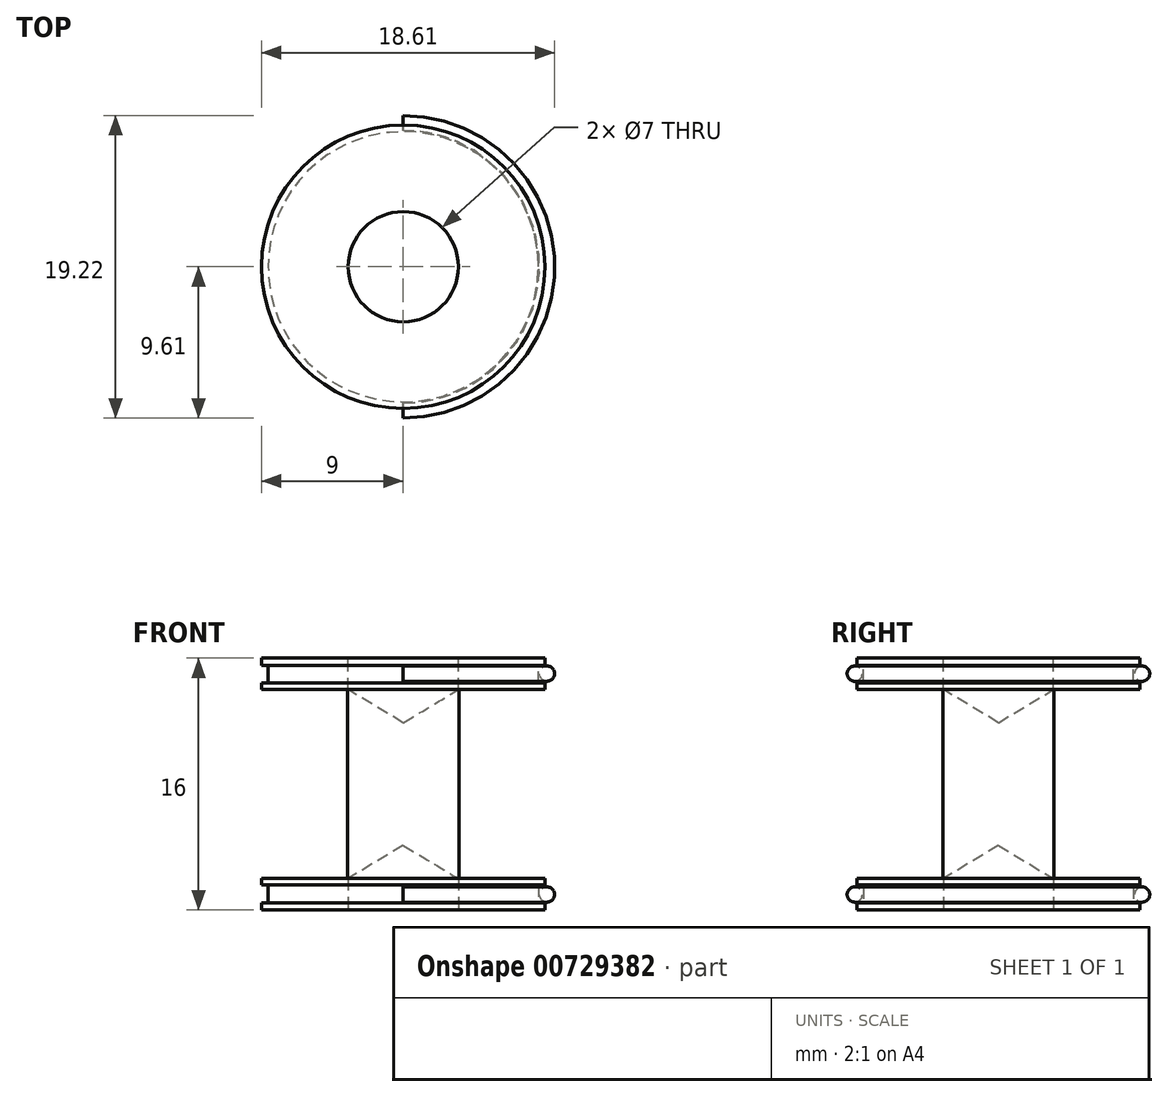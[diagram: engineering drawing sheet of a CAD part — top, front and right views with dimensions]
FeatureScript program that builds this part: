
annotation { "Feature Type Name" : "Feature", "Feature Type Description" : "" }
export const myFeature = defineFeature(function(context is Context, id is Id, definition is map)
    precondition{}
    {
        {
            var Q0;
            Q0=qCreatedBy(makeId("Top.planeOp"),FACE);
            var sketch = newSketch(context, id + "F0", { "sketchPlane" : qUnion([Q0])});
            skCircle(sketch, "E0", {"center": v(0, 0) * mm, "radius": 9 * mm});
            skSolve(sketch);
        }
        {
            var Q0;
            Q0=makeQuery(id+"F0.imprint","IMPRINT",FACE,{"disambiguationData":[TD([[makeQuery(id+"F0.imprint","IMPRINT",EDGE,{"derivedFrom":sQuery(id+"F0.wireOp",EDGE,"E0")}),1.0]])]});
            extrude(context, id + "F1", {"entities" : qUnion([Q0]), "depth" : 2 * mm, "offsetDistance" : 25 * mm});
        }
        {
            var Q0;
            Q0=qCreatedBy(makeId("Right.planeOp"),FACE);
            var sketch = newSketch(context, id + "F2", { "sketchPlane" : qUnion([Q0])});
            skLineSegment(sketch, "E1.bottom", {"start": v(8.58, 1.53) * mm, "end": v(9.56, 1.53) * mm});
            skLineSegment(sketch, "E1.top", {"start": v(8.58, 0.42) * mm, "end": v(9.56, 0.42) * mm});
            skLineSegment(sketch, "E1.left", {"start": v(8.58, 1.53) * mm, "end": v(8.58, 0.42) * mm});
            skLineSegment(sketch, "E1.right", {"start": v(9.56, 1.53) * mm, "end": v(9.56, 0.42) * mm});
            skSolve(sketch);
        }
        {
            var Q0;
            Q0=qCreatedBy(makeId("Top.planeOp"),FACE);
            cPlane(context, id + "F3", {"entities" : qUnion([Q0]), "cplaneType" : CPlaneType.OFFSET, "offset" : 1 * mm, "width" : 150 * mm, "height" : 150 * mm});
        }
        {
            var Q0;
            Q0=qCreatedBy(id+"F3.planeOp",FACE);
            var sketch = newSketch(context, id + "F4", { "sketchPlane" : qUnion([Q0])});
            skCircle(sketch, "E2", {"center": v(0, 0) * mm, "radius": 9 * mm});
            skSolve(sketch);
        }
        {
            var Q0;
            Q0 = qSketchRegion(id + "F2", true);
            var Q1;
            Q1=sQuery(id+"F4.wireOp",EDGE,"E2");
            sweep(context, id + "F5", {"operationType" : NewBodyOperationType.REMOVE, "profiles" : qUnion([Q0]), "path" : qUnion([Q1])});
        }
        {
            var Q0;
            Q0=qCreatedBy(makeId("Right.planeOp"),FACE);
            var sketch = newSketch(context, id + "F6", { "sketchPlane" : qUnion([Q0])});
            skCircle(sketch, "E3", {"center": v(9.13, 1.01) * mm, "radius": 0.48 * mm});
            skSolve(sketch);
        }
        {
            var Q0;
            Q0=qCreatedBy(id+"F3.planeOp",FACE);
            var sketch = newSketch(context, id + "F7", { "sketchPlane" : qUnion([Q0])});
            skArc(sketch, "E4", {"start": v(0, 9) * mm, "mid": v(9, 0) * mm, "end": v(0, -9) * mm});
            skSolve(sketch);
        }
        {
            var Q0;
            Q0=makeQuery(id+"F6.imprint","IMPRINT",FACE,{"disambiguationData":[TD([[makeQuery(id+"F6.imprint","IMPRINT",EDGE,{"derivedFrom":sQuery(id+"F6.wireOp",EDGE,"E3")}),1.0]])]});
            var Q1;
            Q1 = qConstructionFilter(qBodyType(qCreatedBy(id + "F7" ,EDGE), BodyType.WIRE), ConstructionObject.NO);
            sweep(context, id + "F8", {"profiles" : qUnion([Q0]), "path" : qUnion([Q1])});
        }
        {
            var Q0;
            Q0=qCreatedBy(makeId("Top.planeOp"),FACE);
            var sketch = newSketch(context, id + "F9", { "sketchPlane" : qUnion([Q0])});
            skCircle(sketch, "E5", {"center": v(0, 0) * mm, "radius": 3.53 * mm});
            skSolve(sketch);
        }
        {
            var Q0;
            Q0=makeQuery(id+"F9.imprint","IMPRINT",FACE,{"disambiguationData":[TD([[makeQuery(id+"F9.imprint","IMPRINT",EDGE,{"derivedFrom":sQuery(id+"F9.wireOp",EDGE,"E5")}),1.0]])]});
            var Q1;
            Q1=sQuery(id+"F9.wireOp",EDGE,"E5");
            extrude(context, id + "F10", {"entities" : qUnion([Q0]), "surfaceEntities" : qUnion([Q1]), "oppositeDirection" : true, "depth" : 6 * mm, "offsetDistance" : 25 * mm});
        }
        {
            var Q0;
            Q0=makeQuery(id+"F10.opExtrude","CAP_FACE",FACE,{"disambiguationData":[OSD([sQuery(id+"F9.wireOp",EDGE,"E5")])],"isStart":false});
            cPlane(context, id + "F11", {"entities" : qUnion([Q0]), "cplaneType" : CPlaneType.OFFSET, "offset" : 0 * mm, "width" : 150 * mm, "height" : 150 * mm});
        }
        {
            var Q0;
            Q0=makeQuery(id+"F1.opExtrude","CAP_FACE",FACE,{"disambiguationData":[OSD([sQuery(id+"F0.wireOp",EDGE,"E0")])],"isStart":false});
            var sketch = newSketch(context, id + "F12", { "sketchPlane" : qUnion([Q0])});
            skLineSegment(sketch, "E6", {"start": v(0, 0) * mm, "end": v(4.9, 0) * mm});
            skSolve(sketch);
        }
        {
            var Q0;
            Q0=sQuery(id+"F12.wireOp",VERTEX,"E6.start");
            var Q1;
            Q1=makeQuery(id+"F1.opExtrude","SWEPT_BODY",BODY,{"disambiguationData":[OSD([sQuery(id+"F0.wireOp",EDGE,"E0")])]});
            var Q2;
            Q2=makeQuery(id+"F10.opExtrude","SWEPT_BODY",BODY,{"disambiguationData":[OSD([sQuery(id+"F9.wireOp",EDGE,"E5")])]});
            hole(context, id + "F13", {"style" : HoleStyle.SIMPLE, "endStyle" : HoleEndStyle.BLIND, "holeDiameter" : 7 * mm, "majorDiameter" : 5 * mm, "holeDepth" : 2 * mm, "isTappedThrough" : true, "tappedDepth" : 12 * mm, "tapClearance" : 3, "locations" : qUnion([Q0]), "scope" : qUnion([Q1, Q2])});
        }
        {
            var Q0;
            Q0=makeQuery(id+"F10.opExtrude","SWEPT_BODY",BODY,{"disambiguationData":[OSD([sQuery(id+"F9.wireOp",EDGE,"E5")])]});
            var Q1;
            Q1=makeQuery(id+"F8.opSweep","SWEPT_BODY",BODY,{"disambiguationData":[OSD([sQuery(id+"F6.wireOp",EDGE,"E3"),sQuery(id+"F7.wireOp",EDGE,"E4")])]});
            var Q2;
            Q2=makeQuery(id+"F1.opExtrude","SWEPT_BODY",BODY,{"disambiguationData":[OSD([sQuery(id+"F0.wireOp",EDGE,"E0")])]});
            var Q3;
            Q3=qCreatedBy(id+"F11.planeOp",FACE);
            mirror(context, id + "F14", {"operationType" : NewBodyOperationType.ADD, "entities" : qUnion([Q0, Q1, Q2]), "mirrorPlane" : qUnion([Q3])});
        }
    });
